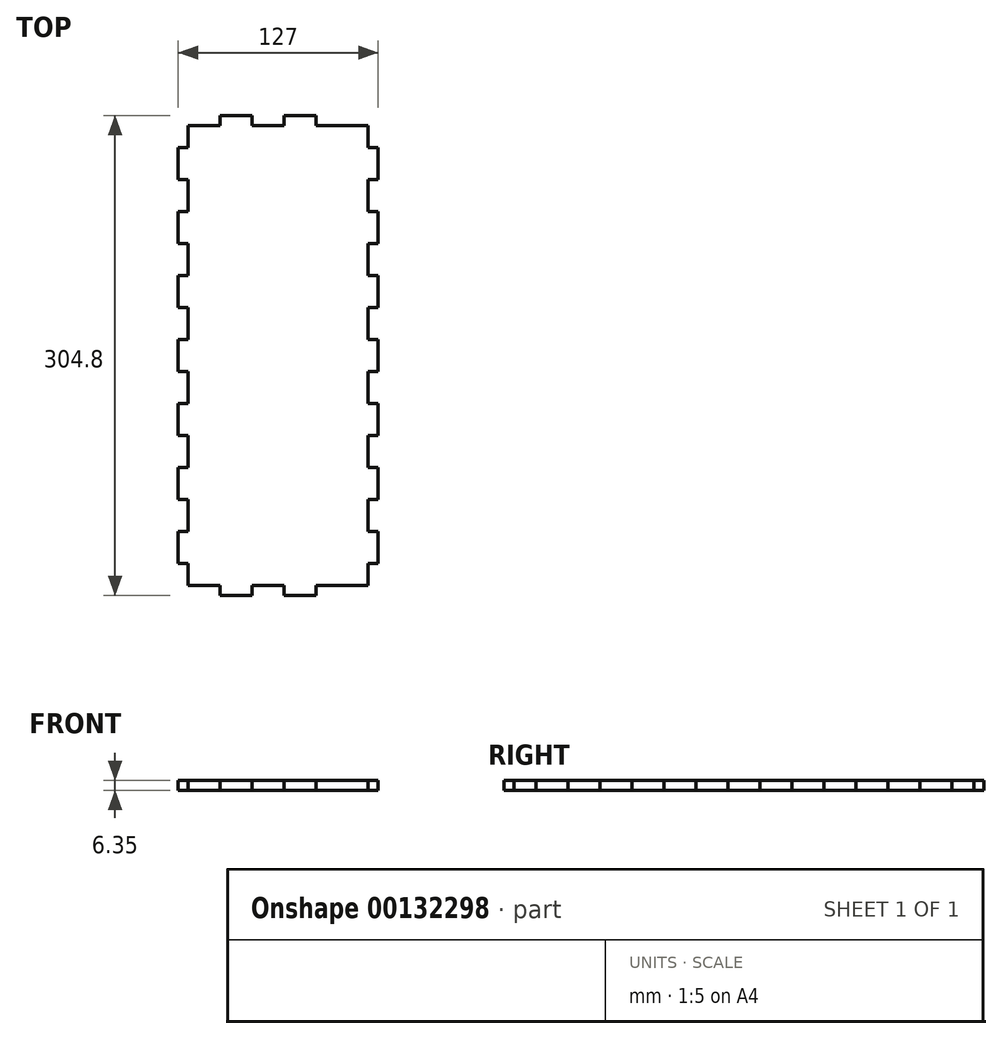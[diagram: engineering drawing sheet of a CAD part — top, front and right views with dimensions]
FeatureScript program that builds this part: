
annotation { "Feature Type Name" : "Feature", "Feature Type Description" : "" }
export const myFeature = defineFeature(function(context is Context, id is Id, definition is map)
    precondition{}
    {
        {
            var Q0;
            Q0=qCreatedBy(makeId("Top.planeOp"),FACE);
            var sketch = newSketch(context, id + "F0", { "sketchPlane" : qUnion([Q0])});
            skLineSegment(sketch, "E0", {"start": v(0, 59.4) * mm, "end": v(0, 0) * mm, "construction": true});
            skLineSegment(sketch, "E1", {"start": v(0, 0) * mm, "end": v(59.72, 0) * mm, "construction": true});
            skLineSegment(sketch, "E2.bottom", {"start": v(-76.2, 146.05) * mm, "end": v(63.5, 146.05) * mm, "construction": true});
            skLineSegment(sketch, "E2.left", {"start": v(-76.2, 146.05) * mm, "end": v(-76.2, -146.05) * mm, "construction": true});
            skLineSegment(sketch, "E2.right", {"start": v(63.5, 146.05) * mm, "end": v(63.5, -146.05) * mm, "construction": true});
            skLineSegment(sketch, "E3", {"start": v(57.15, 146.05) * mm, "end": v(57.15, 132.08) * mm});
            skLineSegment(sketch, "E4", {"start": v(57.15, 132.08) * mm, "end": v(63.5, 132.08) * mm});
            skLineSegment(sketch, "E5", {"start": v(63.5, 132.08) * mm, "end": v(63.5, 111.76) * mm});
            skLineSegment(sketch, "E6", {"start": v(63.5, 111.76) * mm, "end": v(57.15, 111.76) * mm});
            skLineSegment(sketch, "E7", {"start": v(57.15, 111.76) * mm, "end": v(57.15, 91.44) * mm});
            skLineSegment(sketch, "E8.0.1.0", {"start": v(57.15, 71.12) * mm, "end": v(57.15, 50.8) * mm});
            skLineSegment(sketch, "E8.0.1.1", {"start": v(57.15, 91.44) * mm, "end": v(63.5, 91.44) * mm});
            skLineSegment(sketch, "E8.0.1.2", {"start": v(63.5, 71.12) * mm, "end": v(57.15, 71.12) * mm});
            skLineSegment(sketch, "E8.0.1.3", {"start": v(63.5, 91.44) * mm, "end": v(63.5, 71.12) * mm});
            skLineSegment(sketch, "E8.0.2.0", {"start": v(57.15, 30.48) * mm, "end": v(57.15, 10.16) * mm});
            skLineSegment(sketch, "E8.0.2.1", {"start": v(57.15, 50.8) * mm, "end": v(63.5, 50.8) * mm});
            skLineSegment(sketch, "E8.0.2.2", {"start": v(63.5, 30.48) * mm, "end": v(57.15, 30.48) * mm});
            skLineSegment(sketch, "E8.0.2.3", {"start": v(63.5, 50.8) * mm, "end": v(63.5, 30.48) * mm});
            skLineSegment(sketch, "E8.0.3.0", {"start": v(57.15, -10.16) * mm, "end": v(57.15, -30.48) * mm});
            skLineSegment(sketch, "E8.0.3.1", {"start": v(57.15, 10.16) * mm, "end": v(63.5, 10.16) * mm});
            skLineSegment(sketch, "E8.0.3.2", {"start": v(63.5, -10.16) * mm, "end": v(57.15, -10.16) * mm});
            skLineSegment(sketch, "E8.0.3.3", {"start": v(63.5, 10.16) * mm, "end": v(63.5, -10.16) * mm});
            skLineSegment(sketch, "E8.0.4.0", {"start": v(57.15, -50.8) * mm, "end": v(57.15, -71.12) * mm});
            skLineSegment(sketch, "E8.0.4.1", {"start": v(57.15, -30.48) * mm, "end": v(63.5, -30.48) * mm});
            skLineSegment(sketch, "E8.0.4.2", {"start": v(63.5, -50.8) * mm, "end": v(57.15, -50.8) * mm});
            skLineSegment(sketch, "E8.0.4.3", {"start": v(63.5, -30.48) * mm, "end": v(63.5, -50.8) * mm});
            skLineSegment(sketch, "E8.0.5.0", {"start": v(57.15, -91.44) * mm, "end": v(57.15, -111.76) * mm});
            skLineSegment(sketch, "E8.0.5.1", {"start": v(57.15, -71.12) * mm, "end": v(63.5, -71.12) * mm});
            skLineSegment(sketch, "E8.0.5.2", {"start": v(63.5, -91.44) * mm, "end": v(57.15, -91.44) * mm});
            skLineSegment(sketch, "E8.0.5.3", {"start": v(63.5, -71.12) * mm, "end": v(63.5, -91.44) * mm});
            skLineSegment(sketch, "E8.0.6.0", {"start": v(57.15, -132.08) * mm, "end": v(57.15, -146.05) * mm});
            skLineSegment(sketch, "E8.0.6.1", {"start": v(57.15, -111.76) * mm, "end": v(63.5, -111.76) * mm});
            skLineSegment(sketch, "E8.0.6.2", {"start": v(63.5, -132.08) * mm, "end": v(57.15, -132.08) * mm});
            skLineSegment(sketch, "E8.0.6.3", {"start": v(63.5, -111.76) * mm, "end": v(63.5, -132.08) * mm});
            skLineSegment(sketch, "E8.direction1", {"start": v(57.15, 91.44) * mm, "end": v(95.25, 91.44) * mm, "construction": true});
            skLineSegment(sketch, "E8.direction2", {"start": v(57.15, 91.44) * mm, "end": v(57.15, 50.8) * mm, "construction": true});
            skLineSegment(sketch, "E9.MirrorCS", {"start": v(-57.15, 132.08) * mm, "end": v(-63.5, 132.08) * mm});
            skLineSegment(sketch, "E10.MirrorCS", {"start": v(-57.15, -111.76) * mm, "end": v(-63.5, -111.76) * mm});
            skLineSegment(sketch, "E11.MirrorCS", {"start": v(-63.5, -10.16) * mm, "end": v(-57.15, -10.16) * mm});
            skLineSegment(sketch, "E12.MirrorCS", {"start": v(-57.15, -30.48) * mm, "end": v(-63.5, -30.48) * mm});
            skLineSegment(sketch, "E13.MirrorCS", {"start": v(-57.15, -71.12) * mm, "end": v(-63.5, -71.12) * mm});
            skLineSegment(sketch, "E14.MirrorCS", {"start": v(-63.5, 111.76) * mm, "end": v(-57.15, 111.76) * mm});
            skLineSegment(sketch, "E15.MirrorCS", {"start": v(-57.15, 91.44) * mm, "end": v(-63.5, 91.44) * mm});
            skLineSegment(sketch, "E16.MirrorCS", {"start": v(-63.5, 71.12) * mm, "end": v(-57.15, 71.12) * mm});
            skLineSegment(sketch, "E17.MirrorCS", {"start": v(-63.5, -50.8) * mm, "end": v(-57.15, -50.8) * mm});
            skLineSegment(sketch, "E18.MirrorCS", {"start": v(-63.5, 30.48) * mm, "end": v(-57.15, 30.48) * mm});
            skLineSegment(sketch, "E19.MirrorCS", {"start": v(-63.5, -132.08) * mm, "end": v(-57.15, -132.08) * mm});
            skLineSegment(sketch, "E20.MirrorCS", {"start": v(-63.5, -91.44) * mm, "end": v(-57.15, -91.44) * mm});
            skLineSegment(sketch, "E21.MirrorCS", {"start": v(-57.15, 10.16) * mm, "end": v(-63.5, 10.16) * mm});
            skLineSegment(sketch, "E22.MirrorCS", {"start": v(-57.15, 50.8) * mm, "end": v(-63.5, 50.8) * mm});
            skLineSegment(sketch, "E23.MirrorCS", {"start": v(-57.15, 146.05) * mm, "end": v(-57.15, 132.08) * mm});
            skLineSegment(sketch, "E24.MirrorCS", {"start": v(-63.5, 91.44) * mm, "end": v(-63.5, 71.12) * mm});
            skLineSegment(sketch, "E25.MirrorCS", {"start": v(-63.5, -30.48) * mm, "end": v(-63.5, -50.8) * mm});
            skLineSegment(sketch, "E26.MirrorCS", {"start": v(-57.15, -10.16) * mm, "end": v(-57.15, -30.48) * mm});
            skLineSegment(sketch, "E27.MirrorCS", {"start": v(-63.5, -111.76) * mm, "end": v(-63.5, -132.08) * mm});
            skLineSegment(sketch, "E28.MirrorCS", {"start": v(-57.15, 91.44) * mm, "end": v(-95.25, 91.44) * mm, "construction": true});
            skLineSegment(sketch, "E29.MirrorCS", {"start": v(-63.5, -71.12) * mm, "end": v(-63.5, -91.44) * mm});
            skLineSegment(sketch, "E30.MirrorCS", {"start": v(-63.5, 146.05) * mm, "end": v(-63.5, -146.05) * mm, "construction": true});
            skLineSegment(sketch, "E31.MirrorCS", {"start": v(-63.5, 132.08) * mm, "end": v(-63.5, 111.76) * mm});
            skLineSegment(sketch, "E32.MirrorCS", {"start": v(-63.5, 50.8) * mm, "end": v(-63.5, 30.48) * mm});
            skLineSegment(sketch, "E33.MirrorCS", {"start": v(-57.15, 111.76) * mm, "end": v(-57.15, 91.44) * mm});
            skLineSegment(sketch, "E34.MirrorCS", {"start": v(-57.15, 71.12) * mm, "end": v(-57.15, 50.8) * mm});
            skLineSegment(sketch, "E35.MirrorCS", {"start": v(-57.15, -91.44) * mm, "end": v(-57.15, -111.76) * mm});
            skLineSegment(sketch, "E36.MirrorCS", {"start": v(-57.15, -50.8) * mm, "end": v(-57.15, -71.12) * mm});
            skLineSegment(sketch, "E37.MirrorCS", {"start": v(-63.5, 10.16) * mm, "end": v(-63.5, -10.16) * mm});
            skLineSegment(sketch, "E38.MirrorCS", {"start": v(-57.15, 30.48) * mm, "end": v(-57.15, 10.16) * mm});
            skLineSegment(sketch, "E39.MirrorCS", {"start": v(-57.15, 91.44) * mm, "end": v(-57.15, 50.8) * mm, "construction": true});
            skLineSegment(sketch, "E40.MirrorCS", {"start": v(76.2, -146.05) * mm, "end": v(-63.5, -146.05) * mm, "construction": true});
            skLineSegment(sketch, "E41", {"start": v(-57.15, -132.08) * mm, "end": v(-57.15, -146.05) * mm});
            skLineSegment(sketch, "E42", {"start": v(-57.15, 146.05) * mm, "end": v(-36.83, 146.05) * mm});
            skLineSegment(sketch, "E43", {"start": v(-36.83, 146.05) * mm, "end": v(-36.83, 152.4) * mm});
            skLineSegment(sketch, "E44", {"start": v(-36.83, 152.4) * mm, "end": v(-16.51, 152.4) * mm});
            skLineSegment(sketch, "E45", {"start": v(-16.51, 152.4) * mm, "end": v(-16.51, 146.05) * mm});
            skLineSegment(sketch, "E46.1.0.0", {"start": v(24.13, 152.4) * mm, "end": v(24.13, 146.05) * mm});
            skLineSegment(sketch, "E46.1.0.1", {"start": v(3.8, 152.4) * mm, "end": v(24.13, 152.4) * mm});
            skLineSegment(sketch, "E46.1.0.2", {"start": v(3.8, 146.05) * mm, "end": v(3.8, 152.4) * mm});
            skLineSegment(sketch, "E46.1.0.3", {"start": v(-16.51, 146.05) * mm, "end": v(3.8, 146.05) * mm});
            skLineSegment(sketch, "E46.direction1", {"start": v(-57.15, 146.05) * mm, "end": v(-16.51, 146.05) * mm, "construction": true});
            skLineSegment(sketch, "E47", {"start": v(24.13, 146.05) * mm, "end": v(57.15, 146.05) * mm});
            skLineSegment(sketch, "E48.MirrorCS", {"start": v(-36.83, -146.05) * mm, "end": v(-36.83, -152.4) * mm});
            skLineSegment(sketch, "E49.MirrorCS", {"start": v(24.13, -152.4) * mm, "end": v(24.13, -146.05) * mm});
            skLineSegment(sketch, "E50.MirrorCS", {"start": v(3.8, -146.05) * mm, "end": v(3.8, -152.4) * mm});
            skLineSegment(sketch, "E51.MirrorCS", {"start": v(-16.51, -152.4) * mm, "end": v(-16.51, -146.05) * mm});
            skLineSegment(sketch, "E52.MirrorCS", {"start": v(-57.15, -146.05) * mm, "end": v(-36.83, -146.05) * mm});
            skLineSegment(sketch, "E53.MirrorCS", {"start": v(3.8, -152.4) * mm, "end": v(24.13, -152.4) * mm});
            skLineSegment(sketch, "E54.MirrorCS", {"start": v(-57.15, -146.05) * mm, "end": v(-16.51, -146.05) * mm, "construction": true});
            skLineSegment(sketch, "E55.MirrorCS", {"start": v(-16.51, -146.05) * mm, "end": v(3.8, -146.05) * mm});
            skLineSegment(sketch, "E56.MirrorCS", {"start": v(24.13, -146.05) * mm, "end": v(57.15, -146.05) * mm});
            skLineSegment(sketch, "E57.MirrorCS", {"start": v(-36.83, -152.4) * mm, "end": v(-16.51, -152.4) * mm});
            skSolve(sketch);
        }
        {
            var Q0;
            Q0 = qSketchRegion(id + "F0", true);
            extrude(context, id + "F1", {"entities" : qUnion([Q0]), "depth" : 6.35 * mm});
        }
    });
